# Revit family: Plumbing Fixture_Water Heater_Stiebel Eltron_SHC
name_source: partatom
category: Plumbing Fixtures
revit_build: Autodesk Revit 2015 (Build: 20140223_1515(x64)
units: mm (PartAtom-declared; Revit-internal decimal feet)

## types (2) — shared parameters
ApparentLoad_ANZRS = 2400 VA
CW Connection = Yes
HW Connection = Yes
Manufacturer = Stiebel Eltron
Type Comments = Instantaneous Water Heater
URL = http://www.stiebel.com.au
Vent Connection = No
Waste Connection = No

## per-type parameters (varying)
| type | Description | Manufacturer_Overall Depth | Manufacturer_Overall Height | Manufacturer_Overall Width | Manufacturer_Spec Code | Model | Type Name |
| 10 AU | Compact Under Sink Point of Use Water Heater - 10 Litre | 270 mm  [stored 0.885827 ft] | 403 mm  [stored 1.32218 ft] | 280 mm  [stored 0.918635 ft] | SHC 10 AU | SHC 10 AU | SHC_280x403x270 : 10 AU |
| 15 AU | Compact Under Sink Point of Use Water Heater - 15 Litre | 318 mm  [stored 1.04331 ft] | 429 mm  [stored 1.40748 ft] | 320 mm  [stored 1.04987 ft] | SHC 15 AU | SHC 15 AU | SHC_320x429x318 : 15 AU |

note: [stored X ft] marks values corroborated as IEEE doubles in the binary element streams (Revit-internal decimal feet)

## geometry (parser evidence)
native form markers: Sweep x5
no freeform markers — native parametric forms only
